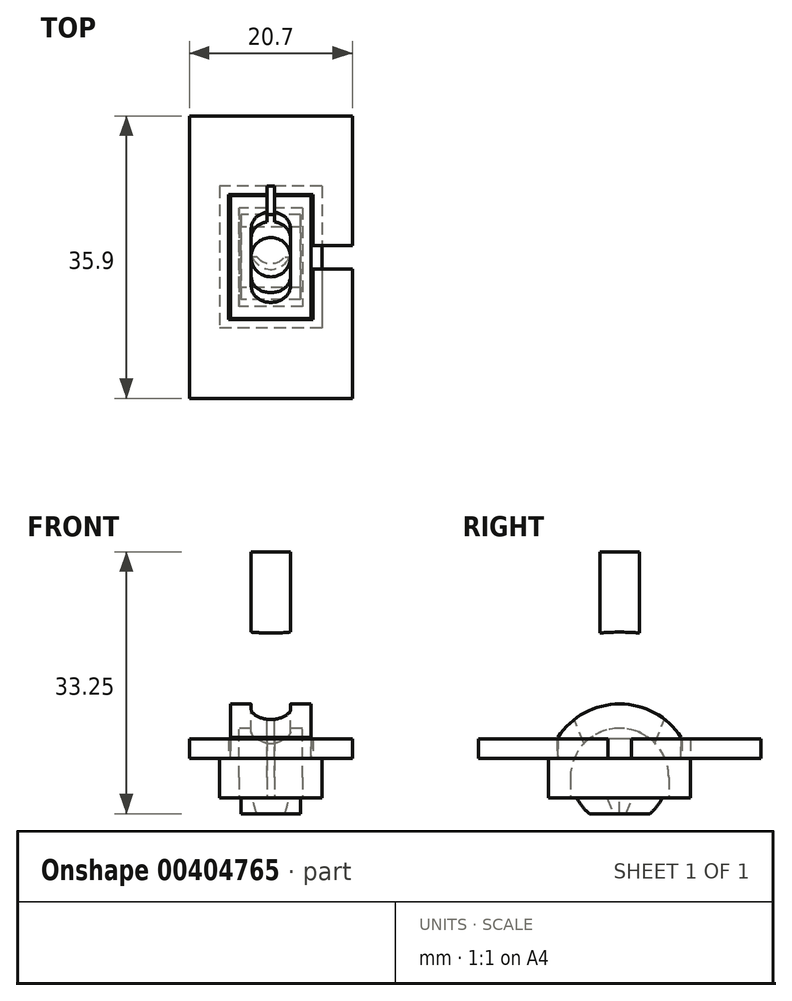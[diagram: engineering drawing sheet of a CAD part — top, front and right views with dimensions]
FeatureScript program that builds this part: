
annotation { "Feature Type Name" : "Feature", "Feature Type Description" : "" }
export const myFeature = defineFeature(function(context is Context, id is Id, definition is map)
    precondition{}
    {
        {
            var Q0;
            Q0=qCreatedBy(makeId("Front.planeOp"),FACE);
            var sketch = newSketch(context, id + "F0", { "sketchPlane" : qUnion([Q0])});
            skLineSegment(sketch, "E0.bottom", {"start": v(-10.35, 17.95) * mm, "end": v(10.35, 17.95) * mm});
            skLineSegment(sketch, "E0.top", {"start": v(-10.35, -17.95) * mm, "end": v(10.35, -17.95) * mm});
            skLineSegment(sketch, "E0.left", {"start": v(-10.35, 17.95) * mm, "end": v(-10.35, -17.95) * mm});
            skLineSegment(sketch, "E0.right", {"start": v(10.35, 17.95) * mm, "end": v(10.35, 1.5) * mm});
            skPoint(sketch, "E0.middle", {"position": v(0, 0) * mm});
            skLineSegment(sketch, "E1.bottom", {"start": v(-5.35, 7.95) * mm, "end": v(5.35, 7.95) * mm});
            skLineSegment(sketch, "E1.top", {"start": v(-5.35, -7.95) * mm, "end": v(5.35, -7.95) * mm});
            skLineSegment(sketch, "E1.left", {"start": v(-5.35, 7.95) * mm, "end": v(-5.35, -7.95) * mm});
            skLineSegment(sketch, "E1.right", {"start": v(5.35, 7.95) * mm, "end": v(5.35, 1.5) * mm});
            skLineSegment(sketch, "E2", {"start": v(5.35, 1.5) * mm, "end": v(10.35, 1.5) * mm});
            skLineSegment(sketch, "E3", {"start": v(10.35, -1.5) * mm, "end": v(5.35, -1.5) * mm});
            skLineSegment(sketch, "E4.trimOffspring", {"start": v(10.35, -1.5) * mm, "end": v(10.35, -17.95) * mm});
            skLineSegment(sketch, "E5.trimOffspring", {"start": v(5.35, -1.5) * mm, "end": v(5.35, -7.95) * mm});
            skSolve(sketch);
        }
        {
            var Q0;
            Q0 = qSketchRegion(id + "F0", true);
            extrude(context, id + "F1", {"entities" : qUnion([Q0]), "depth" : 2.5 * mm, "symmetric" : true});
        }
        {
            var Q0;
            Q0=makeQuery(id+"F1.opExtrude","CAP_FACE",FACE,{"disambiguationData":[OSD([sQuery(id+"F0.wireOp",EDGE,"E0.bottom"),sQuery(id+"F0.wireOp",EDGE,"E0.top"),sQuery(id+"F0.wireOp",EDGE,"E0.left"),sQuery(id+"F0.wireOp",EDGE,"E0.right"),sQuery(id+"F0.wireOp",EDGE,"E1.bottom"),sQuery(id+"F0.wireOp",EDGE,"E1.top"),sQuery(id+"F0.wireOp",EDGE,"E1.left"),sQuery(id+"F0.wireOp",EDGE,"E1.right"),sQuery(id+"F0.wireOp",EDGE,"E2"),sQuery(id+"F0.wireOp",EDGE,"E3"),sQuery(id+"F0.wireOp",EDGE,"E4.trimOffspring"),sQuery(id+"F0.wireOp",EDGE,"E5.trimOffspring")])],"isStart":true});
            var sketch = newSketch(context, id + "F2", { "sketchPlane" : qUnion([Q0])});
            skLineSegment(sketch, "E6.bottom", {"start": v(-6.5, 9) * mm, "end": v(6.5, 9) * mm});
            skLineSegment(sketch, "E6.top", {"start": v(-6.5, -9) * mm, "end": v(6.5, -9) * mm});
            skLineSegment(sketch, "E6.left", {"start": v(-6.5, 9) * mm, "end": v(-6.5, -9) * mm});
            skLineSegment(sketch, "E6.right", {"start": v(6.5, 9) * mm, "end": v(6.5, -9) * mm});
            skPoint(sketch, "E6.middle", {"position": v(0, 0) * mm});
            skSolve(sketch);
        }
        {
            var Q0;
            Q0 = qSketchRegion(id + "F2", true);
            extrude(context, id + "F3", {"entities" : qUnion([Q0]), "depth" : 5 * mm});
        }
        {
            var Q0;
            Q0=qCreatedBy(makeId("Right.planeOp"),FACE);
            var sketch = newSketch(context, id + "F4", { "sketchPlane" : qUnion([Q0])});
            skArc(sketch, "E7", {"start": v(8.25, 3.85) * mm, "mid": v(-2.35, 0) * mm, "end": v(8.25, -3.85) * mm});
            skLineSegment(sketch, "E8", {"start": v(8.25, -3.85) * mm, "end": v(8.25, 3.85) * mm});
            skSolve(sketch);
        }
        {
            var Q0;
            Q0 = qSketchRegion(id + "F4", true);
            extrude(context, id + "F5", {"entities" : qUnion([Q0]), "depth" : 7.6 * mm, "symmetric" : true});
        }
        {
            var Q0;
            Q0=qCreatedBy(makeId("Front.planeOp"),FACE);
            var sketch = newSketch(context, id + "F6", { "sketchPlane" : qUnion([Q0])});
            skCircle(sketch, "E9", {"center": v(0, 0) * mm, "radius": 2.5 * mm});
            skSolve(sketch);
        }
        {
            var Q0;
            Q0 = qSketchRegion(id + "F6", true);
            extrude(context, id + "F7", {"entities" : qUnion([Q0]), "operationType" : NewBodyOperationType.ADD, "depth" : 25 * mm});
        }
        {
            var Q0;
            Q0=makeQuery(id+"F1.opExtrude","SWEPT_FACE",FACE,{"disambiguationData":[OSD([sQuery(id+"F0.wireOp",EDGE,"E1.left")])]});
            cPlane(context, id + "F8", {"entities" : qUnion([Q0]), "cplaneType" : CPlaneType.OFFSET, "offset" : 0.25 * mm, "width" : 150 * mm, "height" : 150 * mm});
        }
        {
            var Q0;
            Q0=makeQuery(id+"F1.opExtrude","SWEPT_FACE",FACE,{"disambiguationData":[OSD([sQuery(id+"F0.wireOp",EDGE,"E1.right")])]});
            cPlane(context, id + "F9", {"entities" : qUnion([Q0]), "cplaneType" : CPlaneType.OFFSET, "offset" : 0.25 * mm, "width" : 150 * mm, "height" : 150 * mm});
        }
        {
            var Q0;
            Q0=qCreatedBy(id+"F8.planeOp",FACE);
            var sketch = newSketch(context, id + "F10", { "sketchPlane" : qUnion([Q0])});
            skArc(sketch, "E10.0.0", {"start": v(8.25, 3.85) * mm, "mid": v(-2.35, 0) * mm, "end": v(8.25, -3.85) * mm, "construction": true});
            skLineSegment(sketch, "E10.0.1", {"start": v(8.25, -3.85) * mm, "end": v(8.25, 3.85) * mm, "construction": true});
            skArc(sketch, "E11", {"start": v(-1.45, 7.82) * mm, "mid": v(-5.69, 0) * mm, "end": v(-1.45, -7.83) * mm});
            skLineSegment(sketch, "E12.0.1", {"start": v(1.25, -7.95) * mm, "end": v(-1.25, -7.95) * mm, "construction": true});
            skLineSegment(sketch, "E12.0.3", {"start": v(-1.25, -7.95) * mm, "end": v(1.25, -7.95) * mm, "construction": true});
            skLineSegment(sketch, "E13.0", {"start": v(1.25, 7.95) * mm, "end": v(1.25, -7.95) * mm, "construction": true});
            skLineSegment(sketch, "E14.0", {"start": v(-1.25, 7.95) * mm, "end": v(1.25, 7.95) * mm, "construction": true});
            skLineSegment(sketch, "E15", {"start": v(-1.45, -7.83) * mm, "end": v(1.25, -7.83) * mm});
            skLineSegment(sketch, "E16", {"start": v(1.25, -7.83) * mm, "end": v(1.25, 7.82) * mm});
            skLineSegment(sketch, "E17", {"start": v(1.25, 7.82) * mm, "end": v(-1.45, 7.82) * mm});
            skSolve(sketch);
        }
        {
            var Q0;
            Q0 = qSketchRegion(id + "F10", true);
            var Q1;
            Q1=qCreatedBy(id+"F9.planeOp",FACE);
            extrude(context, id + "F11", {"entities" : qUnion([Q0]), "operationType" : NewBodyOperationType.ADD, "endBound" : BoundingType.UP_TO_SURFACE, "endBoundEntityFace" : qUnion([Q1]), "depth" : 25 * mm});
        }
        {
            var Q0;
            Q0=makeQuery(id+"F5.opExtrude","CAP_FACE",FACE,{"disambiguationData":[OSD([sQuery(id+"F4.wireOp",EDGE,"E7"),sQuery(id+"F4.wireOp",EDGE,"E8")])],"isStart":true});
            cPlane(context, id + "F12", {"entities" : qUnion([Q0]), "cplaneType" : CPlaneType.OFFSET, "offset" : .25 * mm, "width" : 150 * mm, "height" : 150 * mm});
        }
        {
            var Q0;
            Q0=makeQuery(id+"F5.opExtrude","CAP_FACE",FACE,{"disambiguationData":[OSD([sQuery(id+"F4.wireOp",EDGE,"E7"),sQuery(id+"F4.wireOp",EDGE,"E8")])],"isStart":false});
            cPlane(context, id + "F13", {"entities" : qUnion([Q0]), "cplaneType" : CPlaneType.OFFSET, "offset" : .25 * mm, "width" : 150 * mm, "height" : 150 * mm});
        }
        {
            var Q0;
            Q0=qCreatedBy(id+"F12.planeOp",FACE);
            var sketch = newSketch(context, id + "F14", { "sketchPlane" : qUnion([Q0])});
            skArc(sketch, "E18.0.0", {"start": v(-8.25, -3.85) * mm, "mid": v(2.35, 0) * mm, "end": v(-8.25, 3.85) * mm, "construction": true});
            skLineSegment(sketch, "E18.0.1", {"start": v(-8.25, 3.85) * mm, "end": v(-8.25, -3.85) * mm, "construction": true});
            skArc(sketch, "E19.0", {"start": v(-3.65, -6.25) * mm, "mid": v(2.6, 0) * mm, "end": v(-3.65, 6.25) * mm});
            skLineSegment(sketch, "E20", {"start": v(-3.65, 6.25) * mm, "end": v(-6.25, 6.25) * mm});
            skLineSegment(sketch, "E21", {"start": v(-3.65, -6.25) * mm, "end": v(-6.25, -6.25) * mm});
            skLineSegment(sketch, "E22", {"start": v(-6.25, 6.25) * mm, "end": v(-6.25, -6.25) * mm});
            skSolve(sketch);
        }
        {
            var Q0;
            Q0 = qSketchRegion(id + "F14", true);
            var Q1;
            Q1=qCreatedBy(id+"F13.planeOp",FACE);
            extrude(context, id + "F15", {"entities" : qUnion([Q0]), "operationType" : NewBodyOperationType.REMOVE, "endBound" : BoundingType.UP_TO_SURFACE, "oppositeDirection" : true, "endBoundEntityFace" : qUnion([Q1]), "depth" : 25 * mm});
        }
        {
            var Q0;
            Q0=qCreatedBy(makeId("Right.planeOp"),FACE);
            var sketch = newSketch(context, id + "F16", { "sketchPlane" : qUnion([Q0])});
            skLineSegment(sketch, "E23", {"start": v(3.65, 0) * mm, "end": v(-13.76, 7.2) * mm, "construction": true});
            skLineSegment(sketch, "E24", {"start": v(3.65, 0) * mm, "end": v(-13.76, -7.2) * mm, "construction": true});
            skLineSegment(sketch, "E25", {"start": v(10.18, 0) * mm, "end": v(-12.91, 9.57) * mm});
            skLineSegment(sketch, "E26", {"start": v(10.18, 0) * mm, "end": v(-12.91, -9.57) * mm});
            skArc(sketch, "E27", {"start": v(-12.91, -9.57) * mm, "mid": v(-14.82, 0) * mm, "end": v(-12.91, 9.57) * mm});
            skSolve(sketch);
        }
        {
            var Q0;
            Q0 = qSketchRegion(id + "F16", true);
            extrude(context, id + "F17", {"entities" : qUnion([Q0]), "operationType" : NewBodyOperationType.REMOVE, "oppositeDirection" : true, "depth" : 5 * mm, "symmetric" : true});
        }
        {
            var Q0;
            Q0=makeQuery(id+"F17.boolean.opBoolean","COPY",EDGE,{"derivedFrom":makeQuery(id+"F17.opExtrude","CAP_EDGE",EDGE,{"disambiguationData":[OSD([sQuery(id+"F16.wireOp",EDGE,"E26")])],"isStart":true})});
            var Q1;
            Q1=makeQuery(id+"F17.boolean.opBoolean","COPY",EDGE,{"derivedFrom":makeQuery(id+"F17.opExtrude","CAP_EDGE",EDGE,{"disambiguationData":[OSD([sQuery(id+"F16.wireOp",EDGE,"E26")])],"isStart":false})});
            var Q2;
            Q2=makeQuery(id+"F17.boolean.opBoolean","COPY",EDGE,{"derivedFrom":makeQuery(id+"F17.opExtrude","CAP_EDGE",EDGE,{"disambiguationData":[OSD([sQuery(id+"F16.wireOp",EDGE,"E25")])],"isStart":false})});
            var Q3;
            Q3=makeQuery(id+"F17.boolean.opBoolean","COPY",EDGE,{"derivedFrom":makeQuery(id+"F17.opExtrude","CAP_EDGE",EDGE,{"disambiguationData":[OSD([sQuery(id+"F16.wireOp",EDGE,"E25")])],"isStart":true})});
            fillet(context, id + "F18", {"entities" : qUnion([Q0, Q1, Q2, Q3]), "radius" : 2.5 * mm, "tangentPropagation" : true, "allowEdgeOverflow" : false});
        }
        {
            var Q0;
            Q0=makeQuery(id+"F3.opExtrude","SWEPT_FACE",FACE,{"disambiguationData":[OSD([sQuery(id+"F2.wireOp",EDGE,"E6.bottom")])]});
            var sketch = newSketch(context, id + "F19", { "sketchPlane" : qUnion([Q0])});
            skLineSegment(sketch, "E28.bottom", {"start": v(-0.5, 6.25) * mm, "end": v(0.5, 6.25) * mm});
            skLineSegment(sketch, "E28.top", {"start": v(-0.5, -25) * mm, "end": v(0.5, -25) * mm});
            skLineSegment(sketch, "E28.left", {"start": v(-0.5, -25) * mm, "end": v(-0.5, 6.25) * mm});
            skLineSegment(sketch, "E28.right", {"start": v(0.5, -25) * mm, "end": v(0.5, 6.25) * mm});
            skSolve(sketch);
        }
        {
            var Q0;
            Q0 = qSketchRegion(id + "F19", true);
            var Q1;
            Q1=makeQuery(id+"F18.opFillet","BLEND_FACE",FACE,{"disambiguationData":[OSD([sQuery(id+"F16.wireOp",EDGE,"E25")])]});
            extrude(context, id + "F20", {"entities" : qUnion([Q0]), "operationType" : NewBodyOperationType.REMOVE, "endBound" : BoundingType.UP_TO_SURFACE, "oppositeDirection" : true, "endBoundEntityFace" : qUnion([Q1]), "depth" : 25 * mm});
        }
        {
            var Q0;
            Q0=makeQuery(id+"F3.opExtrude","SWEPT_BODY",BODY,{"disambiguationData":[OSD([sQuery(id+"F2.wireOp",EDGE,"7412d821-1f8e-40f6-9bc5-06c474f9c141.0"),sQuery(id+"F2.wireOp",EDGE,"7412d821-1f8e-40f6-9bc5-06c474f9c141.1"),sQuery(id+"F2.wireOp",EDGE,"7412d821-1f8e-40f6-9bc5-06c474f9c141.2"),sQuery(id+"F2.wireOp",EDGE,"7412d821-1f8e-40f6-9bc5-06c474f9c141.3"),sQuery(id+"F2.wireOp",EDGE,"E6.bottom"),sQuery(id+"F2.wireOp",EDGE,"E6.top"),sQuery(id+"F2.wireOp",EDGE,"E6.left"),sQuery(id+"F2.wireOp",EDGE,"E6.right")])]});
            var Q1;
            Q1=makeQuery(id+"F1.opExtrude","SWEPT_BODY",BODY,{"disambiguationData":[OSD([sQuery(id+"F0.wireOp",EDGE,"E0.bottom"),sQuery(id+"F0.wireOp",EDGE,"E0.top"),sQuery(id+"F0.wireOp",EDGE,"E0.left"),sQuery(id+"F0.wireOp",EDGE,"E0.right"),sQuery(id+"F0.wireOp",EDGE,"E1.bottom"),sQuery(id+"F0.wireOp",EDGE,"E1.top"),sQuery(id+"F0.wireOp",EDGE,"E1.left"),sQuery(id+"F0.wireOp",EDGE,"E1.right"),sQuery(id+"F0.wireOp",EDGE,"E2"),sQuery(id+"F0.wireOp",EDGE,"E3"),sQuery(id+"F0.wireOp",EDGE,"E4.trimOffspring"),sQuery(id+"F0.wireOp",EDGE,"E5.trimOffspring")])]});
            var Q2;
            Q2=makeQuery(id+"F5.opExtrude","SWEPT_BODY",BODY,{"disambiguationData":[OSD([sQuery(id+"F4.wireOp",EDGE,"E7")])]});
            var Q3;
            Q3=makeQuery(id+"F1.opExtrude","CAP_EDGE",EDGE,{"disambiguationData":[OSD([sQuery(id+"F0.wireOp",EDGE,"E0.top")])],"isStart":true});
            transform(context, id + "F21", {"entities" : qUnion([Q0, Q1, Q2]), "transformType" : TransformType.ROTATION, "transformAxis" : qUnion([Q3]), "angle" : 90 * degree, "oppositeDirection" : true, "makeCopy" : false});
        }
    });
